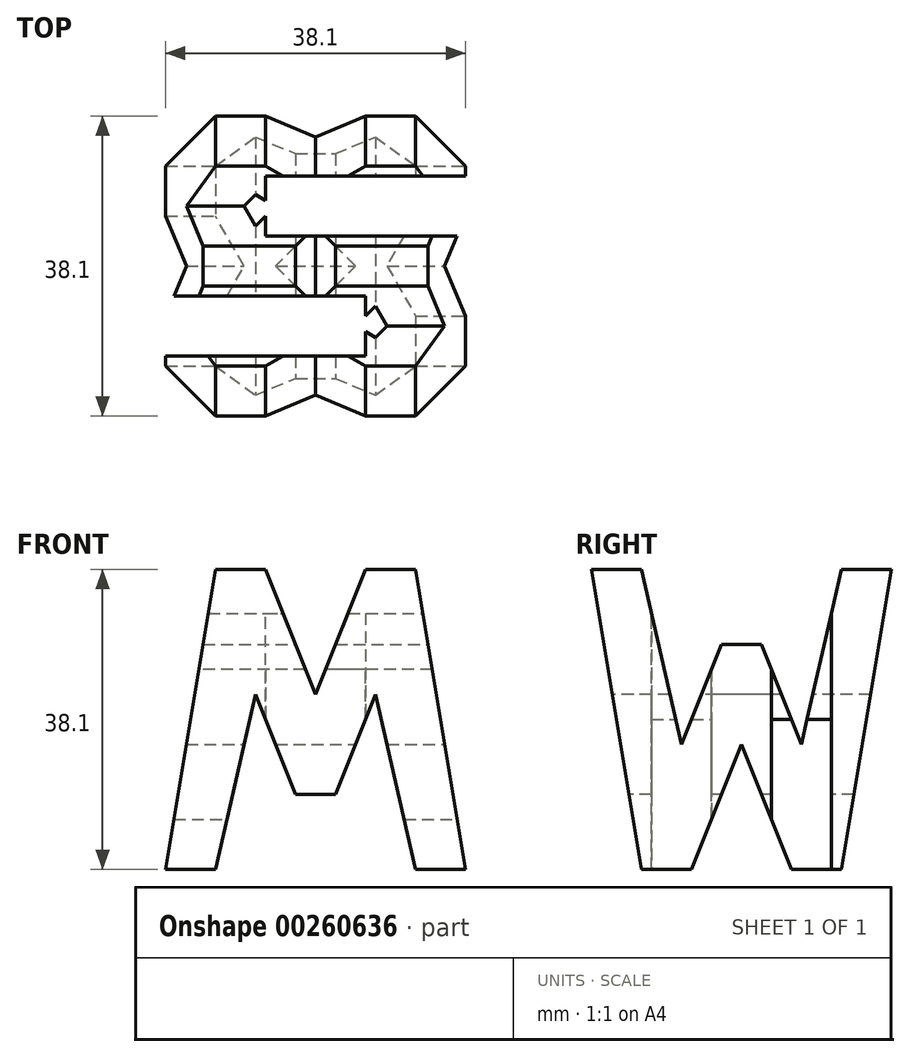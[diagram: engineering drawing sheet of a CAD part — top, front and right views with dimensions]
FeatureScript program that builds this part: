
annotation { "Feature Type Name" : "Feature", "Feature Type Description" : "" }
export const myFeature = defineFeature(function(context is Context, id is Id, definition is map)
    precondition{}
    {
        {
            var Q0;
            Q0=qCreatedBy(makeId("Front.planeOp"),FACE);
            var sketch = newSketch(context, id + "F0", { "sketchPlane" : qUnion([Q0])});
            skLineSegment(sketch, "E0", {"start": v(0, 0) * mm, "end": v(0, 38.1) * mm});
            skLineSegment(sketch, "E1", {"start": v(0, 0) * mm, "end": v(38.1, 0) * mm});
            skLineSegment(sketch, "E2", {"start": v(0, 38.1) * mm, "end": v(38.1, 38.1) * mm});
            skLineSegment(sketch, "E3", {"start": v(38.1, 38.1) * mm, "end": v(38.1, 0) * mm});
            skSolve(sketch);
        }
        {
            var Q0;
            Q0=makeQuery(id+"F0.imprint","IMPRINT",FACE,{"disambiguationData":[TD([[makeQuery(id+"F0.imprint","IMPRINT",EDGE,{"derivedFrom":sQuery(id+"F0.wireOp",EDGE,"E0")}),-1.0]])]});
            extrude(context, id + "F1", {"entities" : qUnion([Q0]), "depth" : 38.1 * mm});
        }
        {
            var Q0;
            Q0=qCreatedBy(makeId("Front.planeOp"),FACE);
            cPlane(context, id + "F2", {"entities" : qUnion([Q0]), "cplaneType" : CPlaneType.OFFSET, "offset" : 38.1 * mm, "width" : 152.4 * mm, "height" : 152.4 * mm});
        }
        {
            var Q0;
            Q0=qCreatedBy(makeId("Right.planeOp"),FACE);
            cPlane(context, id + "F3", {"entities" : qUnion([Q0]), "cplaneType" : CPlaneType.OFFSET, "offset" : 38.1 * mm, "width" : 152.4 * mm, "height" : 152.4 * mm});
        }
        {
            var Q0;
            Q0=qCreatedBy(makeId("Top.planeOp"),FACE);
            cPlane(context, id + "F4", {"entities" : qUnion([Q0]), "cplaneType" : CPlaneType.OFFSET, "offset" : 38.1 * mm, "width" : 152.4 * mm, "height" : 152.4 * mm});
        }
        {
            var Q0;
            Q0=qCreatedBy(id+"F3.planeOp",FACE);
            var sketch = newSketch(context, id + "F5", { "sketchPlane" : qUnion([Q0])});
            skLineSegment(sketch, "E4", {"start": v(0, 0) * mm, "end": v(0, 38.1) * mm});
            skPoint(sketch, "E5.start.orphan", {"position": v(-38.1, 0) * mm});
            skLineSegment(sketch, "E6", {"start": v(0, 38.1) * mm, "end": v(-38.1, 38.1) * mm});
            skLineSegment(sketch, "E7", {"start": v(-38.1, 38.1) * mm, "end": v(-38.1, 0) * mm});
            skLineSegment(sketch, "E8", {"start": v(-38.1, 0) * mm, "end": v(-31.75, 0) * mm});
            skLineSegment(sketch, "E9", {"start": v(-38.1, 38.1) * mm, "end": v(-31.75, 0) * mm});
            skLineSegment(sketch, "E10", {"start": v(-31.75, 38.1) * mm, "end": v(-26.67, 15.87) * mm});
            skLineSegment(sketch, "E11", {"start": v(-26.67, 15.87) * mm, "end": v(-21.59, 28.58) * mm});
            skLineSegment(sketch, "E12", {"start": v(-21.59, 28.58) * mm, "end": v(-16.5, 28.58) * mm});
            skLineSegment(sketch, "E13", {"start": v(-16.5, 28.58) * mm, "end": v(-11.43, 15.88) * mm});
            skLineSegment(sketch, "E14", {"start": v(-11.43, 15.88) * mm, "end": v(-6.35, 38.1) * mm});
            skLineSegment(sketch, "E15", {"start": v(0, 38.1) * mm, "end": v(-6.35, 0) * mm});
            skLineSegment(sketch, "E16", {"start": v(-12.7, 0) * mm, "end": v(-19.05, 15.88) * mm});
            skLineSegment(sketch, "E17", {"start": v(-19.05, 15.88) * mm, "end": v(-25.4, 0) * mm});
            skLineSegment(sketch, "E18", {"start": v(-31.75, 0) * mm, "end": v(0, 0) * mm});
            skSolve(sketch);
        }
        {
            var Q0;
            {var subQ1=sQuery(id+"F5.wireOp",EDGE,"E10");Q0=makeQuery(id+"F5.imprint","IMPRINT",FACE,{"disambiguationData":[TD([[makeQuery(id+"F5.imprint","IMPRINT",EDGE,{"derivedFrom":subQ1}),1.0]])]});}
            var Q1;
            Q1=makeQuery(id+"F5.imprint","IMPRINT",FACE,{"disambiguationData":[TD([[makeQuery(id+"F5.imprint","IMPRINT",EDGE,{"derivedFrom":sQuery(id+"F5.wireOp",EDGE,"E7")}),1.0]])]});
            var Q2;
            {var subQ0=sQuery(id+"F5.wireOp",EDGE,"E16");Q2=makeQuery(id+"F5.imprint","IMPRINT",FACE,{"disambiguationData":[TD([[makeQuery(id+"F5.imprint","IMPRINT",EDGE,{"derivedFrom":subQ0}),1.0]])]});}
            var Q3;
            {var subQ0=sQuery(id+"F5.wireOp",EDGE,"E4");Q3=makeQuery(id+"F5.imprint","IMPRINT",FACE,{"disambiguationData":[TD([[makeQuery(id+"F5.imprint","IMPRINT",EDGE,{"derivedFrom":subQ0}),1.0]])]});}
            extrude(context, id + "F6", {"entities" : qUnion([Q0, Q1, Q2, Q3]), "operationType" : NewBodyOperationType.REMOVE, "oppositeDirection" : true, "depth" : 38.1 * mm});
        }
        {
            var Q0;
            Q0=qCreatedBy(id+"F2.planeOp",FACE);
            var sketch = newSketch(context, id + "F7", { "sketchPlane" : qUnion([Q0])});
            skLineSegment(sketch, "E19", {"start": v(0, 38.1) * mm, "end": v(0, 0) * mm});
            skLineSegment(sketch, "E20", {"start": v(0, 0) * mm, "end": v(6.35, 0) * mm});
            skLineSegment(sketch, "E21", {"start": v(38.1, 0) * mm, "end": v(38.1, 38.1) * mm});
            skLineSegment(sketch, "E22", {"start": v(38.1, 38.1) * mm, "end": v(0, 38.1) * mm});
            skLineSegment(sketch, "E23", {"start": v(12.7, 38.1) * mm, "end": v(19.05, 22.23) * mm});
            skLineSegment(sketch, "E24", {"start": v(19.05, 22.23) * mm, "end": v(25.4, 38.1) * mm});
            skLineSegment(sketch, "E25", {"start": v(31.75, 38.1) * mm, "end": v(38.1, 0) * mm});
            skLineSegment(sketch, "E26", {"start": v(6.35, 38.1) * mm, "end": v(0, 0) * mm});
            skLineSegment(sketch, "E27", {"start": v(6.35, 0) * mm, "end": v(11.43, 22.23) * mm});
            skLineSegment(sketch, "E28", {"start": v(11.43, 22.23) * mm, "end": v(16.51, 9.52) * mm});
            skLineSegment(sketch, "E29", {"start": v(16.51, 9.53) * mm, "end": v(21.6, 9.53) * mm});
            skLineSegment(sketch, "E30", {"start": v(21.59, 9.53) * mm, "end": v(26.67, 22.23) * mm});
            skLineSegment(sketch, "E31", {"start": v(26.67, 22.23) * mm, "end": v(31.75, 0) * mm});
            skLineSegment(sketch, "E32", {"start": v(31.75, 0) * mm, "end": v(38.1, 0) * mm});
            skLineSegment(sketch, "E33", {"start": v(6.35, 38.1) * mm, "end": v(0, 38.1) * mm});
            skLineSegment(sketch, "E34", {"start": v(6.35, 0) * mm, "end": v(31.75, 0) * mm});
            skLineSegment(sketch, "E35", {"start": v(31.75, 0) * mm, "end": v(26.67, 22.23) * mm});
            skLineSegment(sketch, "E36", {"start": v(21.6, 9.53) * mm, "end": v(16.51, 9.53) * mm});
            skLineSegment(sketch, "E37", {"start": v(16.51, 9.53) * mm, "end": v(11.43, 22.22) * mm});
            skSolve(sketch);
        }
        {
            var Q0;
            {var subQ0=sQuery(id+"F7.wireOp",EDGE,"E23");Q0=makeQuery(id+"F7.imprint","IMPRINT",FACE,{"disambiguationData":[TD([[makeQuery(id+"F7.imprint","IMPRINT",EDGE,{"derivedFrom":subQ0}),1.0]])]});}
            var Q1;
            {var subQ0=sQuery(id+"F7.wireOp",EDGE,"E21");Q1=makeQuery(id+"F7.imprint","IMPRINT",FACE,{"disambiguationData":[TD([[makeQuery(id+"F7.imprint","IMPRINT",EDGE,{"derivedFrom":subQ0}),1.0]])]});}
            var Q2;
            {var subQ0=sQuery(id+"F7.wireOp",EDGE,"E26");Q2=makeQuery(id+"F7.imprint","IMPRINT",FACE,{"disambiguationData":[TD([[makeQuery(id+"F7.imprint","IMPRINT",EDGE,{"derivedFrom":subQ0}),-1.0]])]});}
            var Q3;
            Q3=makeQuery(id+"F7.imprint","IMPRINT",FACE,{"disambiguationData":[TD([[makeQuery(id+"F7.imprint","IMPRINT",EDGE,{"derivedFrom":sQuery(id+"F7.wireOp",EDGE,"E27")}),-1.0]])]});
            extrude(context, id + "F8", {"entities" : qUnion([Q0, Q1, Q2, Q3]), "operationType" : NewBodyOperationType.REMOVE, "oppositeDirection" : true, "depth" : 38.1 * mm});
        }
        {
            var Q0;
            Q0=qCreatedBy(id+"F4.planeOp",FACE);
            var sketch = newSketch(context, id + "F9", { "sketchPlane" : qUnion([Q0])});
            skLineSegment(sketch, "E38", {"start": v(0, 0) * mm, "end": v(38.1, 0) * mm});
            skLineSegment(sketch, "E39", {"start": v(38.1, 0) * mm, "end": v(38.1, -38.1) * mm});
            skLineSegment(sketch, "E40", {"start": v(38.1, -38.1) * mm, "end": v(0, -38.1) * mm});
            skLineSegment(sketch, "E41", {"start": v(0, -38.1) * mm, "end": v(0, 0) * mm});
            skLineSegment(sketch, "E42", {"start": v(38.1, -7.62) * mm, "end": v(12.7, -7.62) * mm});
            skLineSegment(sketch, "E43", {"start": v(12.7, -7.62) * mm, "end": v(12.7, -15.24) * mm});
            skLineSegment(sketch, "E44", {"start": v(12.7, -15.24) * mm, "end": v(38.1, -15.24) * mm});
            skLineSegment(sketch, "E45", {"start": v(0, -22.86) * mm, "end": v(25.4, -22.86) * mm});
            skLineSegment(sketch, "E46", {"start": v(25.4, -22.86) * mm, "end": v(25.4, -30.48) * mm});
            skLineSegment(sketch, "E47", {"start": v(25.4, -30.48) * mm, "end": v(0, -30.48) * mm});
            skSolve(sketch);
        }
        {
            var Q0;
            {var subQ0=sQuery(id+"F9.wireOp",EDGE,"E45");Q0=makeQuery(id+"F9.imprint","IMPRINT",FACE,{"disambiguationData":[TD([[makeQuery(id+"F9.imprint","IMPRINT",EDGE,{"derivedFrom":subQ0}),-1.0]])]});}
            var Q1;
            {var subQ0=sQuery(id+"F9.wireOp",EDGE,"E42");Q1=makeQuery(id+"F9.imprint","IMPRINT",FACE,{"disambiguationData":[TD([[makeQuery(id+"F9.imprint","IMPRINT",EDGE,{"derivedFrom":subQ0}),1.0]])]});}
            extrude(context, id + "F10", {"entities" : qUnion([Q0, Q1]), "operationType" : NewBodyOperationType.REMOVE, "oppositeDirection" : true, "depth" : 38.1 * mm});
        }
    });
